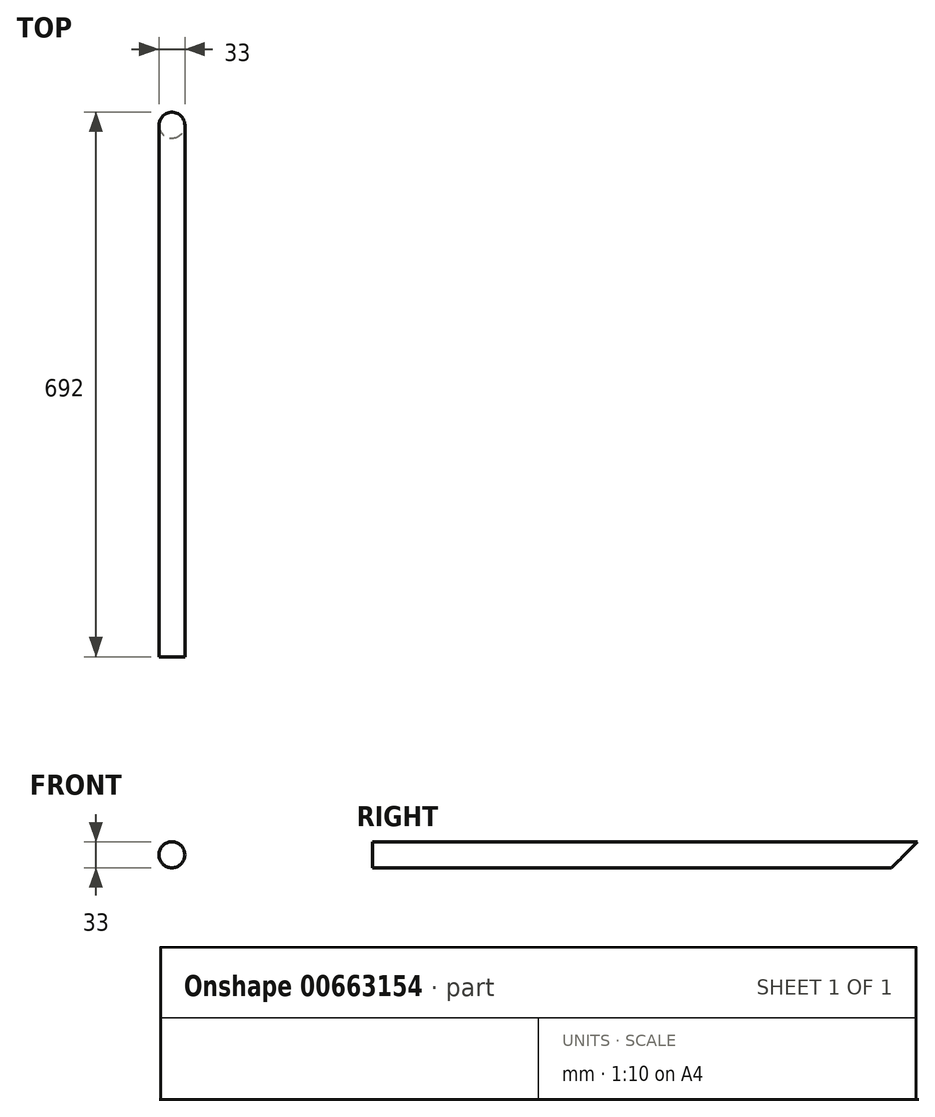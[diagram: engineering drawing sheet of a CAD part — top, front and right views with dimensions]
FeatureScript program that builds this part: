
annotation { "Feature Type Name" : "Feature", "Feature Type Description" : "" }
export const myFeature = defineFeature(function(context is Context, id is Id, definition is map)
    precondition{}
    {
        {
            var Q0;
            Q0=qCreatedBy(makeId("Front.planeOp"),FACE);
            var sketch = newSketch(context, id + "F0", { "sketchPlane" : qUnion([Q0])});
            skLineSegment(sketch, "E0.bottom", {"start": v(16.5, 16.5) * mm, "end": v(-16.5, 16.5) * mm});
            skLineSegment(sketch, "E0.top", {"start": v(16.5, -16.5) * mm, "end": v(-16.5, -16.5) * mm});
            skLineSegment(sketch, "E0.left", {"start": v(16.5, 16.5) * mm, "end": v(16.5, -16.5) * mm});
            skLineSegment(sketch, "E0.right", {"start": v(-16.5, 16.5) * mm, "end": v(-16.5, -16.5) * mm});
            skPoint(sketch, "E0.middle", {"position": v(0, 0) * mm});
            skSolve(sketch);
        }
        {
            var Q0;
            Q0=makeQuery(id+"F0.imprint","IMPRINT",FACE,{"disambiguationData":[TD([[makeQuery(id+"F0.imprint","IMPRINT",EDGE,{"derivedFrom":sQuery(id+"F0.wireOp",EDGE,"E0.bottom")}),1.0]])]});
            extrude(context, id + "F1", {"entities" : qUnion([Q0]), "endBound" : BoundingType.SYMMETRIC, "depth" : (700 - 8) * mm, "offsetDistance" : 25 * mm});
        }
        {
            var Q0;
            Q0=makeQuery(id+"F1.opExtrude","SWEPT_FACE",FACE,{"disambiguationData":[OSD([sQuery(id+"F0.wireOp",EDGE,"E0.left")])]});
            var sketch = newSketch(context, id + "F2", { "sketchPlane" : qUnion([Q0])});
            skLineSegment(sketch, "E1", {"start": v(346, 16.5) * mm, "end": v(313, -16.5) * mm});
            skSolve(sketch);
        }
        {
            var Q0;
            {var subQ0=sQuery(id+"F2.wireOp",EDGE,"E1");Q0=makeQuery(id+"F2.imprint","IMPRINT",FACE,{"disambiguationData":[TD([[makeQuery(id+"F2.imprint","IMPRINT",EDGE,{"derivedFrom":subQ0}),1.0]])]});}
            var Q1;
            {var subQ0=sQuery(id+"F2.wireOp",EDGE,"FPeIgTk1-qAel-Q9xu-tjv9-IDNfBGmjxjwN");Q1=makeQuery(id+"F2.imprint","IMPRINT",FACE,{"disambiguationData":[TD([[makeQuery(id+"F2.imprint","IMPRINT",EDGE,{"derivedFrom":subQ0}),-1.0]])]});}
            extrude(context, id + "F3", {"entities" : qUnion([Q0, Q1]), "operationType" : NewBodyOperationType.REMOVE, "oppositeDirection" : true, "depth" : 50 * mm, "offsetDistance" : 25 * mm});
        }
        {
            var Q0;
            Q0=makeQuery(id+"F1.opExtrude","SWEPT_EDGE",EDGE,{"disambiguationData":[OSD([sQuery(id+"F0.wireOp",EDGE,"E0.bottom"),sQuery(id+"F0.wireOp",EDGE,"E0.left")])]});
            var Q1;
            Q1=makeQuery(id+"F1.opExtrude","SWEPT_EDGE",EDGE,{"disambiguationData":[OSD([sQuery(id+"F0.wireOp",EDGE,"E0.top"),sQuery(id+"F0.wireOp",EDGE,"E0.left")])]});
            var Q2;
            Q2=makeQuery(id+"F1.opExtrude","SWEPT_EDGE",EDGE,{"disambiguationData":[OSD([sQuery(id+"F0.wireOp",EDGE,"E0.top"),sQuery(id+"F0.wireOp",EDGE,"E0.right")])]});
            var Q3;
            Q3=makeQuery(id+"F1.opExtrude","SWEPT_EDGE",EDGE,{"disambiguationData":[OSD([sQuery(id+"F0.wireOp",EDGE,"E0.bottom"),sQuery(id+"F0.wireOp",EDGE,"E0.right")])]});
            fillet(context, id + "F4", {"entities" : qUnion([Q0, Q1, Q2, Q3]), "radius" : (33 / 2) * mm, "tangentPropagation" : true, "allowEdgeOverflow" : false});
        }
    });
